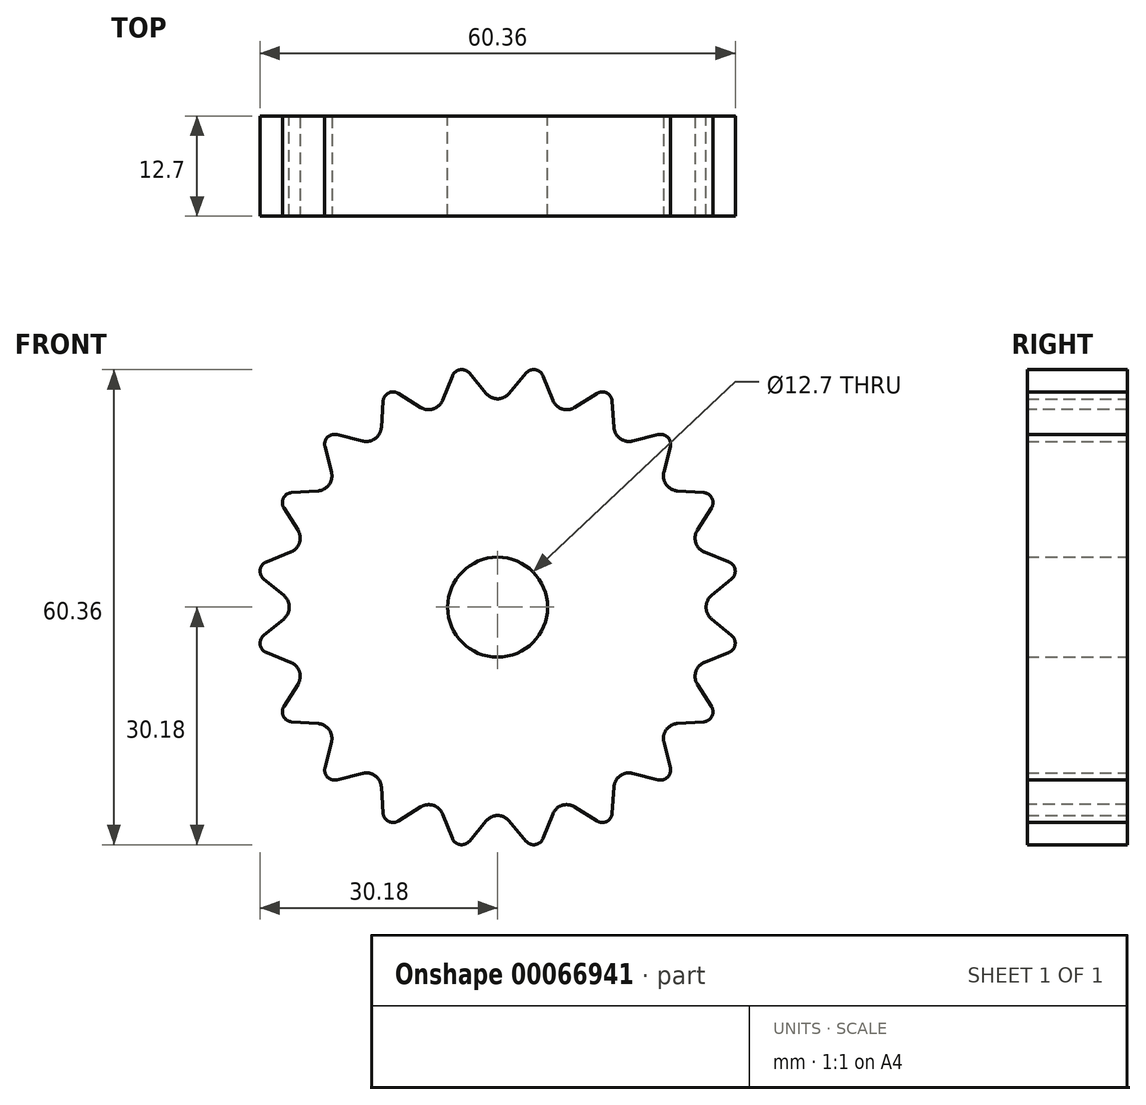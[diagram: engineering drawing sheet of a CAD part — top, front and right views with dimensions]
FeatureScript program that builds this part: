
annotation { "Feature Type Name" : "Feature", "Feature Type Description" : "" }
export const myFeature = defineFeature(function(context is Context, id is Id, definition is map)
    precondition{}
    {
        {
            var Q0;
            Q0=qCreatedBy(makeId("Front.planeOp"),FACE);
            var sketch = newSketch(context, id + "F0", { "sketchPlane" : qUnion([Q0])});
            skCircle(sketch, "E0", {"center": v(0, 0) * mm, "radius": 6.35 * mm});
            skCircle(sketch, "E1", {"center": v(0, 0) * mm, "radius": 25.4 * mm, "construction": true});
            skLineSegment(sketch, "E2", {"start": v(14.93, 20.55) * mm, "end": v(22.45, 22.45) * mm});
            skLineSegment(sketch, "E3", {"start": v(22.45, 22.45) * mm, "end": v(20.55, 14.93) * mm});
            skLineSegment(sketch, "E4", {"start": v(20.55, 14.93) * mm, "end": v(28.29, 14.41) * mm});
            skLineSegment(sketch, "E5", {"start": v(28.29, 14.41) * mm, "end": v(24.16, 7.85) * mm});
            skCircle(sketch, "E6", {"center": v(0, 0) * mm, "radius": 31.75 * mm, "construction": true});
            skLineSegment(sketch, "E7", {"start": v(0, 0) * mm, "end": v(24.16, 7.85) * mm, "construction": true});
            skLineSegment(sketch, "E8", {"start": v(0, 0) * mm, "end": v(20.55, 14.93) * mm, "construction": true});
            skLineSegment(sketch, "E9", {"start": v(0, 0) * mm, "end": v(14.93, 20.55) * mm, "construction": true});
            skLineSegment(sketch, "E10", {"start": v(0, 0) * mm, "end": v(0, 25.4) * mm, "construction": true});
            skLineSegment(sketch, "E11", {"start": v(24.16, 7.85) * mm, "end": v(31.36, 4.97) * mm});
            skLineSegment(sketch, "E12", {"start": v(31.36, 4.97) * mm, "end": v(25.4, 0) * mm});
            skLineSegment(sketch, "E13", {"start": v(0, 0) * mm, "end": v(7.85, 24.16) * mm, "construction": true});
            skLineSegment(sketch, "E14", {"start": v(14.93, 20.55) * mm, "end": v(14.41, 28.29) * mm});
            skLineSegment(sketch, "E15", {"start": v(14.41, 28.29) * mm, "end": v(7.85, 24.16) * mm});
            skLineSegment(sketch, "E16", {"start": v(7.85, 24.16) * mm, "end": v(4.97, 31.36) * mm});
            skLineSegment(sketch, "E17", {"start": v(4.97, 31.36) * mm, "end": v(0, 25.4) * mm});
            skLineSegment(sketch, "E18.MirrorCS", {"start": v(-4.97, 31.36) * mm, "end": v(0, 25.4) * mm});
            skLineSegment(sketch, "E19.MirrorCS", {"start": v(-7.85, 24.16) * mm, "end": v(-4.97, 31.36) * mm});
            skLineSegment(sketch, "E20.MirrorCS", {"start": v(-14.41, 28.29) * mm, "end": v(-7.85, 24.16) * mm});
            skLineSegment(sketch, "E21.MirrorCS", {"start": v(-14.93, 20.55) * mm, "end": v(-14.41, 28.29) * mm});
            skLineSegment(sketch, "E22.MirrorCS", {"start": v(-14.93, 20.55) * mm, "end": v(-22.45, 22.45) * mm});
            skLineSegment(sketch, "E23.MirrorCS", {"start": v(-22.45, 22.45) * mm, "end": v(-20.55, 14.93) * mm});
            skLineSegment(sketch, "E24.MirrorCS", {"start": v(-20.55, 14.93) * mm, "end": v(-28.29, 14.41) * mm});
            skLineSegment(sketch, "E25.MirrorCS", {"start": v(-28.29, 14.41) * mm, "end": v(-24.16, 7.85) * mm});
            skLineSegment(sketch, "E26.MirrorCS", {"start": v(-24.16, 7.85) * mm, "end": v(-31.36, 4.97) * mm});
            skLineSegment(sketch, "E27.MirrorCS", {"start": v(-31.36, 4.97) * mm, "end": v(-25.4, 0) * mm});
            skLineSegment(sketch, "E28.MirrorCS", {"start": v(-31.36, -4.97) * mm, "end": v(-25.4, 0) * mm});
            skLineSegment(sketch, "E29.MirrorCS", {"start": v(-24.16, -7.85) * mm, "end": v(-31.36, -4.97) * mm});
            skLineSegment(sketch, "E30.MirrorCS", {"start": v(-28.29, -14.41) * mm, "end": v(-24.16, -7.85) * mm});
            skLineSegment(sketch, "E31.MirrorCS", {"start": v(-20.55, -14.93) * mm, "end": v(-28.29, -14.41) * mm});
            skLineSegment(sketch, "E32.MirrorCS", {"start": v(-22.45, -22.45) * mm, "end": v(-20.55, -14.93) * mm});
            skLineSegment(sketch, "E33.MirrorCS", {"start": v(-14.93, -20.55) * mm, "end": v(-22.45, -22.45) * mm});
            skLineSegment(sketch, "E34.MirrorCS", {"start": v(-14.41, -28.29) * mm, "end": v(-7.85, -24.16) * mm});
            skLineSegment(sketch, "E35.MirrorCS", {"start": v(-14.93, -20.55) * mm, "end": v(-14.41, -28.29) * mm});
            skLineSegment(sketch, "E36.MirrorCS", {"start": v(-7.85, -24.16) * mm, "end": v(-4.97, -31.36) * mm});
            skLineSegment(sketch, "E37.MirrorCS", {"start": v(-4.97, -31.36) * mm, "end": v(0, -25.4) * mm});
            skLineSegment(sketch, "E38.MirrorCS", {"start": v(4.97, -31.36) * mm, "end": v(0, -25.4) * mm});
            skLineSegment(sketch, "E39.MirrorCS", {"start": v(7.85, -24.16) * mm, "end": v(4.97, -31.36) * mm});
            skLineSegment(sketch, "E40.MirrorCS", {"start": v(14.41, -28.29) * mm, "end": v(7.85, -24.16) * mm});
            skLineSegment(sketch, "E41.MirrorCS", {"start": v(14.93, -20.55) * mm, "end": v(14.41, -28.29) * mm});
            skLineSegment(sketch, "E42.MirrorCS", {"start": v(14.93, -20.55) * mm, "end": v(22.45, -22.45) * mm});
            skLineSegment(sketch, "E43.MirrorCS", {"start": v(22.45, -22.45) * mm, "end": v(20.55, -14.93) * mm});
            skLineSegment(sketch, "E44.MirrorCS", {"start": v(20.55, -14.93) * mm, "end": v(28.29, -14.41) * mm});
            skLineSegment(sketch, "E45.MirrorCS", {"start": v(28.29, -14.41) * mm, "end": v(24.16, -7.85) * mm});
            skLineSegment(sketch, "E46.MirrorCS", {"start": v(24.16, -7.85) * mm, "end": v(31.36, -4.97) * mm});
            skLineSegment(sketch, "E47.MirrorCS", {"start": v(31.36, -4.97) * mm, "end": v(25.4, 0) * mm});
            skSolve(sketch);
        }
        {
            var Q0;
            Q0=makeQuery(id+"F0.imprint","IMPRINT",FACE,{"disambiguationData":[TD([[makeQuery(id+"F0.imprint","IMPRINT",EDGE,{"derivedFrom":sQuery(id+"F0.wireOp",EDGE,"E0")}),-1.0]])]});
            extrude(context, id + "F1", {"entities" : qUnion([Q0]), "depth" : 12.7 * mm});
        }
        {
            var Q0;
            Q0=makeQuery(id+"F1.opExtrude","SWEPT_EDGE",EDGE,{"disambiguationData":[OSD([sQuery(id+"F0.wireOp",EDGE,"E23.MirrorCS"),sQuery(id+"F0.wireOp",EDGE,"E24.MirrorCS")])]});
            var Q1;
            Q1=makeQuery(id+"F1.opExtrude","SWEPT_EDGE",EDGE,{"disambiguationData":[OSD([sQuery(id+"F0.wireOp",EDGE,"E21.MirrorCS"),sQuery(id+"F0.wireOp",EDGE,"E22.MirrorCS")])]});
            var Q2;
            Q2=makeQuery(id+"F1.opExtrude","SWEPT_EDGE",EDGE,{"disambiguationData":[OSD([sQuery(id+"F0.wireOp",EDGE,"E25.MirrorCS"),sQuery(id+"F0.wireOp",EDGE,"E26.MirrorCS")])]});
            var Q3;
            Q3=makeQuery(id+"F1.opExtrude","SWEPT_EDGE",EDGE,{"disambiguationData":[OSD([sQuery(id+"F0.wireOp",EDGE,"E27.MirrorCS"),sQuery(id+"F0.wireOp",EDGE,"E28.MirrorCS")])]});
            var Q4;
            Q4=makeQuery(id+"F1.opExtrude","SWEPT_EDGE",EDGE,{"disambiguationData":[OSD([sQuery(id+"F0.wireOp",EDGE,"E29.MirrorCS"),sQuery(id+"F0.wireOp",EDGE,"E30.MirrorCS")])]});
            var Q5;
            Q5=makeQuery(id+"F1.opExtrude","SWEPT_EDGE",EDGE,{"disambiguationData":[OSD([sQuery(id+"F0.wireOp",EDGE,"E31.MirrorCS"),sQuery(id+"F0.wireOp",EDGE,"E32.MirrorCS")])]});
            var Q6;
            Q6=makeQuery(id+"F1.opExtrude","SWEPT_EDGE",EDGE,{"disambiguationData":[OSD([sQuery(id+"F0.wireOp",EDGE,"E33.MirrorCS"),sQuery(id+"F0.wireOp",EDGE,"E35.MirrorCS")])]});
            var Q7;
            Q7=makeQuery(id+"F1.opExtrude","SWEPT_EDGE",EDGE,{"disambiguationData":[OSD([sQuery(id+"F0.wireOp",EDGE,"E34.MirrorCS"),sQuery(id+"F0.wireOp",EDGE,"E36.MirrorCS")])]});
            var Q8;
            Q8=makeQuery(id+"F1.opExtrude","SWEPT_EDGE",EDGE,{"disambiguationData":[OSD([sQuery(id+"F0.wireOp",EDGE,"E37.MirrorCS"),sQuery(id+"F0.wireOp",EDGE,"E38.MirrorCS")])]});
            var Q9;
            Q9=makeQuery(id+"F1.opExtrude","SWEPT_EDGE",EDGE,{"disambiguationData":[OSD([sQuery(id+"F0.wireOp",EDGE,"E39.MirrorCS"),sQuery(id+"F0.wireOp",EDGE,"E40.MirrorCS")])]});
            var Q10;
            Q10=makeQuery(id+"F1.opExtrude","SWEPT_EDGE",EDGE,{"disambiguationData":[OSD([sQuery(id+"F0.wireOp",EDGE,"E41.MirrorCS"),sQuery(id+"F0.wireOp",EDGE,"E42.MirrorCS")])]});
            var Q11;
            Q11=makeQuery(id+"F1.opExtrude","SWEPT_EDGE",EDGE,{"disambiguationData":[OSD([sQuery(id+"F0.wireOp",EDGE,"E43.MirrorCS"),sQuery(id+"F0.wireOp",EDGE,"E44.MirrorCS")])]});
            var Q12;
            Q12=makeQuery(id+"F1.opExtrude","SWEPT_EDGE",EDGE,{"disambiguationData":[OSD([sQuery(id+"F0.wireOp",EDGE,"E45.MirrorCS"),sQuery(id+"F0.wireOp",EDGE,"E46.MirrorCS")])]});
            var Q13;
            Q13=makeQuery(id+"F1.opExtrude","SWEPT_EDGE",EDGE,{"disambiguationData":[OSD([sQuery(id+"F0.wireOp",EDGE,"E12"),sQuery(id+"F0.wireOp",EDGE,"E47.MirrorCS")])]});
            var Q14;
            Q14=makeQuery(id+"F1.opExtrude","SWEPT_EDGE",EDGE,{"disambiguationData":[OSD([sQuery(id+"F0.wireOp",EDGE,"E5"),sQuery(id+"F0.wireOp",EDGE,"E11")])]});
            var Q15;
            Q15=makeQuery(id+"F1.opExtrude","SWEPT_EDGE",EDGE,{"disambiguationData":[OSD([sQuery(id+"F0.wireOp",EDGE,"E3"),sQuery(id+"F0.wireOp",EDGE,"E4")])]});
            var Q16;
            Q16=makeQuery(id+"F1.opExtrude","SWEPT_EDGE",EDGE,{"disambiguationData":[OSD([sQuery(id+"F0.wireOp",EDGE,"E2"),sQuery(id+"F0.wireOp",EDGE,"E14")])]});
            var Q17;
            Q17=makeQuery(id+"F1.opExtrude","SWEPT_EDGE",EDGE,{"disambiguationData":[OSD([sQuery(id+"F0.wireOp",EDGE,"E15"),sQuery(id+"F0.wireOp",EDGE,"E16")])]});
            var Q18;
            Q18=makeQuery(id+"F1.opExtrude","SWEPT_EDGE",EDGE,{"disambiguationData":[OSD([sQuery(id+"F0.wireOp",EDGE,"E17"),sQuery(id+"F0.wireOp",EDGE,"E18.MirrorCS")])]});
            var Q19;
            Q19=makeQuery(id+"F1.opExtrude","SWEPT_EDGE",EDGE,{"disambiguationData":[OSD([sQuery(id+"F0.wireOp",EDGE,"E19.MirrorCS"),sQuery(id+"F0.wireOp",EDGE,"E20.MirrorCS")])]});
            fillet(context, id + "F2", {"entities" : qUnion([Q0, Q1, Q2, Q3, Q4, Q5, Q6, Q7, Q8, Q9, Q10, Q11, Q12, Q13, Q14, Q15, Q16, Q17, Q18, Q19]), "radius" : 1.9 * mm, "allowEdgeOverflow" : false});
        }
        {
            var Q0;
            Q0=makeQuery(id+"F1.opExtrude","SWEPT_EDGE",EDGE,{"disambiguationData":[OSD([sQuery(id+"F0.wireOp",EDGE,"E44.MirrorCS"),sQuery(id+"F0.wireOp",EDGE,"E45.MirrorCS")])]});
            var Q1;
            Q1=makeQuery(id+"F1.opExtrude","SWEPT_EDGE",EDGE,{"disambiguationData":[OSD([sQuery(id+"F0.wireOp",EDGE,"E42.MirrorCS"),sQuery(id+"F0.wireOp",EDGE,"E43.MirrorCS")])]});
            var Q2;
            Q2=makeQuery(id+"F1.opExtrude","SWEPT_EDGE",EDGE,{"disambiguationData":[OSD([sQuery(id+"F0.wireOp",EDGE,"E40.MirrorCS"),sQuery(id+"F0.wireOp",EDGE,"E41.MirrorCS")])]});
            var Q3;
            Q3=makeQuery(id+"F1.opExtrude","SWEPT_EDGE",EDGE,{"disambiguationData":[OSD([sQuery(id+"F0.wireOp",EDGE,"E38.MirrorCS"),sQuery(id+"F0.wireOp",EDGE,"E39.MirrorCS")])]});
            var Q4;
            Q4=makeQuery(id+"F1.opExtrude","SWEPT_EDGE",EDGE,{"disambiguationData":[OSD([sQuery(id+"F0.wireOp",EDGE,"E34.MirrorCS"),sQuery(id+"F0.wireOp",EDGE,"E35.MirrorCS")])]});
            var Q5;
            Q5=makeQuery(id+"F1.opExtrude","SWEPT_EDGE",EDGE,{"disambiguationData":[OSD([sQuery(id+"F0.wireOp",EDGE,"E36.MirrorCS"),sQuery(id+"F0.wireOp",EDGE,"E37.MirrorCS")])]});
            var Q6;
            Q6=makeQuery(id+"F1.opExtrude","SWEPT_EDGE",EDGE,{"disambiguationData":[OSD([sQuery(id+"F0.wireOp",EDGE,"E32.MirrorCS"),sQuery(id+"F0.wireOp",EDGE,"E33.MirrorCS")])]});
            var Q7;
            Q7=makeQuery(id+"F1.opExtrude","SWEPT_EDGE",EDGE,{"disambiguationData":[OSD([sQuery(id+"F0.wireOp",EDGE,"E30.MirrorCS"),sQuery(id+"F0.wireOp",EDGE,"E31.MirrorCS")])]});
            var Q8;
            Q8=makeQuery(id+"F1.opExtrude","SWEPT_EDGE",EDGE,{"disambiguationData":[OSD([sQuery(id+"F0.wireOp",EDGE,"E28.MirrorCS"),sQuery(id+"F0.wireOp",EDGE,"E29.MirrorCS")])]});
            var Q9;
            Q9=makeQuery(id+"F1.opExtrude","SWEPT_EDGE",EDGE,{"disambiguationData":[OSD([sQuery(id+"F0.wireOp",EDGE,"E26.MirrorCS"),sQuery(id+"F0.wireOp",EDGE,"E27.MirrorCS")])]});
            var Q10;
            Q10=makeQuery(id+"F1.opExtrude","SWEPT_EDGE",EDGE,{"disambiguationData":[OSD([sQuery(id+"F0.wireOp",EDGE,"E20.MirrorCS"),sQuery(id+"F0.wireOp",EDGE,"E21.MirrorCS")])]});
            var Q11;
            Q11=makeQuery(id+"F1.opExtrude","SWEPT_EDGE",EDGE,{"disambiguationData":[OSD([sQuery(id+"F0.wireOp",EDGE,"E18.MirrorCS"),sQuery(id+"F0.wireOp",EDGE,"E19.MirrorCS")])]});
            var Q12;
            Q12=makeQuery(id+"F1.opExtrude","SWEPT_EDGE",EDGE,{"disambiguationData":[OSD([sQuery(id+"F0.wireOp",EDGE,"E24.MirrorCS"),sQuery(id+"F0.wireOp",EDGE,"E25.MirrorCS")])]});
            var Q13;
            Q13=makeQuery(id+"F1.opExtrude","SWEPT_EDGE",EDGE,{"disambiguationData":[OSD([sQuery(id+"F0.wireOp",EDGE,"E22.MirrorCS"),sQuery(id+"F0.wireOp",EDGE,"E23.MirrorCS")])]});
            var Q14;
            Q14=makeQuery(id+"F1.opExtrude","SWEPT_EDGE",EDGE,{"disambiguationData":[OSD([sQuery(id+"F0.wireOp",EDGE,"E16"),sQuery(id+"F0.wireOp",EDGE,"E17")])]});
            var Q15;
            Q15=makeQuery(id+"F1.opExtrude","SWEPT_EDGE",EDGE,{"disambiguationData":[OSD([sQuery(id+"F0.wireOp",EDGE,"E14"),sQuery(id+"F0.wireOp",EDGE,"E15")])]});
            var Q16;
            Q16=makeQuery(id+"F1.opExtrude","SWEPT_EDGE",EDGE,{"disambiguationData":[OSD([sQuery(id+"F0.wireOp",EDGE,"E2"),sQuery(id+"F0.wireOp",EDGE,"E3")])]});
            var Q17;
            Q17=makeQuery(id+"F1.opExtrude","SWEPT_EDGE",EDGE,{"disambiguationData":[OSD([sQuery(id+"F0.wireOp",EDGE,"E4"),sQuery(id+"F0.wireOp",EDGE,"E5")])]});
            var Q18;
            Q18=makeQuery(id+"F1.opExtrude","SWEPT_EDGE",EDGE,{"disambiguationData":[OSD([sQuery(id+"F0.wireOp",EDGE,"E11"),sQuery(id+"F0.wireOp",EDGE,"E12")])]});
            var Q19;
            Q19=makeQuery(id+"F1.opExtrude","SWEPT_EDGE",EDGE,{"disambiguationData":[OSD([sQuery(id+"F0.wireOp",EDGE,"E46.MirrorCS"),sQuery(id+"F0.wireOp",EDGE,"E47.MirrorCS")])]});
            fillet(context, id + "F3", {"entities" : qUnion([Q0, Q1, Q2, Q3, Q4, Q5, Q6, Q7, Q8, Q9, Q10, Q11, Q12, Q13, Q14, Q15, Q16, Q17, Q18, Q19]), "radius" : 1.27 * mm, "tangentPropagation" : true, "allowEdgeOverflow" : false});
        }
    });
